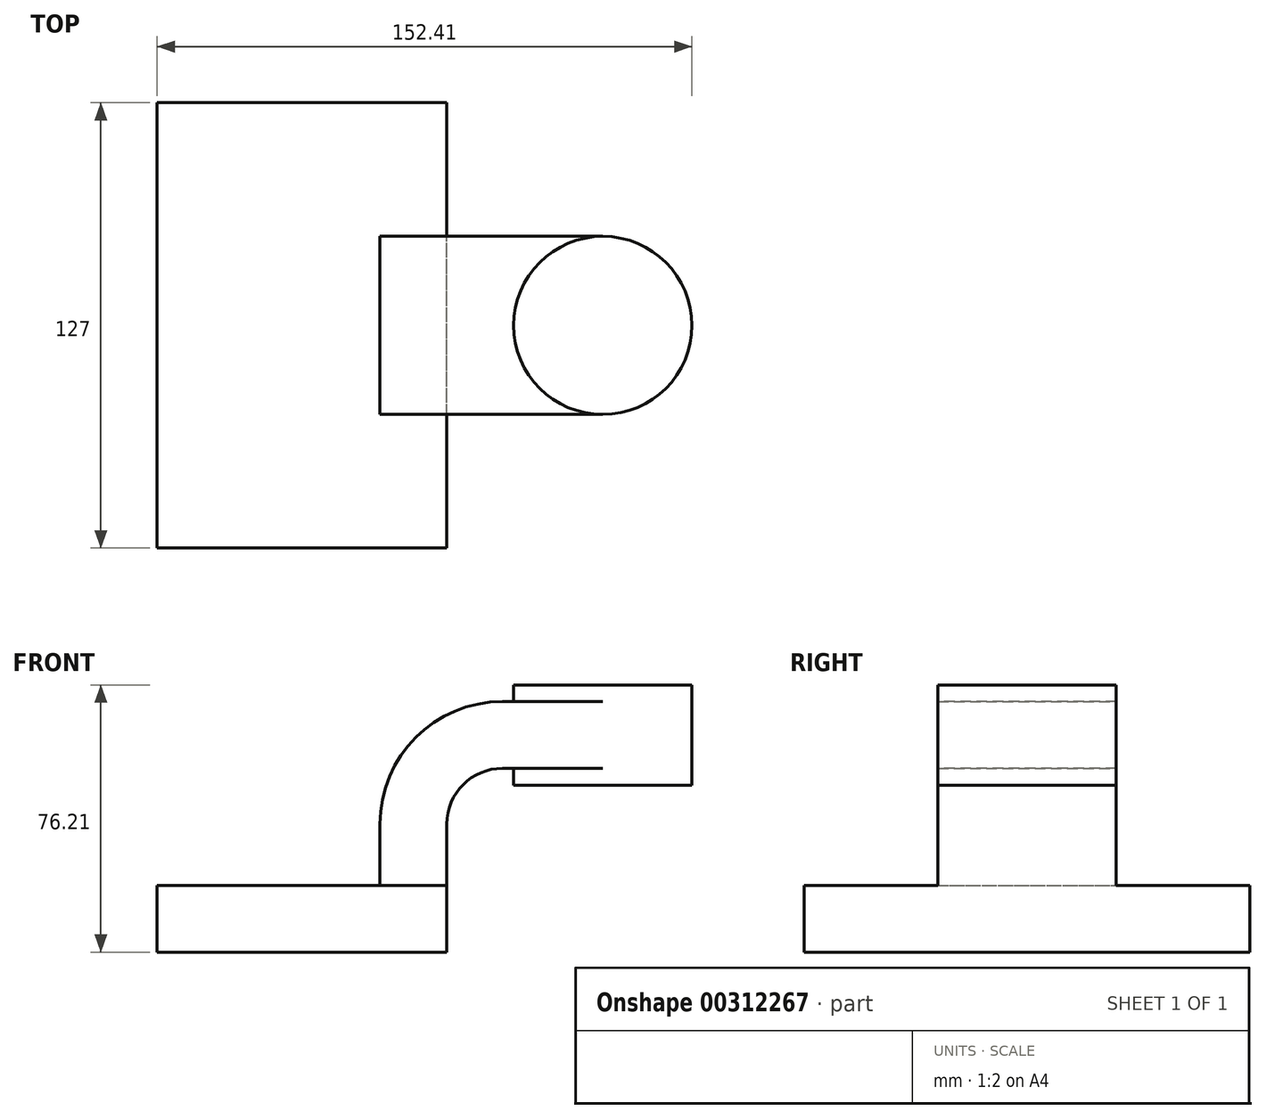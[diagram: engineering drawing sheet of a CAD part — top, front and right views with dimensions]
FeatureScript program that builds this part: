
annotation { "Feature Type Name" : "Feature", "Feature Type Description" : "" }
export const myFeature = defineFeature(function(context is Context, id is Id, definition is map)
    precondition{}
    {
        {
            var Q0;
            Q0=qCreatedBy(makeId("Front.planeOp"),FACE);
            var sketch = newSketch(context, id + "F0", { "sketchPlane" : qUnion([Q0])});
            skLineSegment(sketch, "E0.bottom", {"start": v(41.28, 9.53) * mm, "end": v(-41.28, 9.52) * mm});
            skLineSegment(sketch, "E0.top", {"start": v(41.28, -9.53) * mm, "end": v(-41.28, -9.53) * mm});
            skLineSegment(sketch, "E0.left", {"start": v(41.28, 9.53) * mm, "end": v(41.28, -9.53) * mm});
            skLineSegment(sketch, "E0.right", {"start": v(-41.28, 9.52) * mm, "end": v(-41.28, -9.53) * mm});
            skPoint(sketch, "E0.middle", {"position": v(0, 0) * mm});
            skLineSegment(sketch, "E1.bottom", {"start": v(111.12, 66.68) * mm, "end": v(60.32, 66.68) * mm});
            skLineSegment(sketch, "E1.top", {"start": v(111.12, 38.1) * mm, "end": v(60.32, 38.1) * mm});
            skLineSegment(sketch, "E1.left", {"start": v(111.12, 66.67) * mm, "end": v(111.12, 38.1) * mm});
            skLineSegment(sketch, "E1.right", {"start": v(60.32, 66.67) * mm, "end": v(60.32, 38.1) * mm});
            skPoint(sketch, "E1.middle", {"position": v(85.72, 52.39) * mm});
            skLineSegment(sketch, "E2", {"start": v(41.28, 9.53) * mm, "end": v(41.27, 27) * mm});
            skArc(sketch, "E3", {"start": v(41.27, 27) * mm, "mid": v(45.92, 38.23) * mm, "end": v(57.15, 42.88) * mm});
            skLineSegment(sketch, "E4", {"start": v(57.15, 42.88) * mm, "end": v(85.72, 42.88) * mm});
            skLineSegment(sketch, "E5.0", {"start": v(57.15, 61.93) * mm, "end": v(85.72, 61.93) * mm});
            skArc(sketch, "E5.1", {"start": v(22.22, 27) * mm, "mid": v(32.45, 51.7) * mm, "end": v(57.15, 61.93) * mm});
            skLineSegment(sketch, "E5.2", {"start": v(22.22, 9.52) * mm, "end": v(22.22, 27) * mm});
            skLineSegment(sketch, "E6", {"start": v(85.72, 66.68) * mm, "end": v(85.72, 38.1) * mm});
            skFitSpline(sketch, "E7", {"points": [v(-41.28, 9.52) * mm, v(57.15, 61.93) * mm], "startDerivative": vector(0.43, 51.22) * mm, "endDerivative": vector(140.28, -1.13) * mm});
            skSolve(sketch);
        }
        {
            var Q0;
            Q0=makeQuery(id+"F0.imprint","IMPRINT",FACE,{"disambiguationData":[TD([[makeQuery(id+"F0.imprint","IMPRINT",EDGE,{"derivedFrom":sQuery(id+"F0.wireOp",EDGE,"E0.top")}),-1.0]])]});
            extrude(context, id + "F1", {"entities" : qUnion([Q0]), "endBound" : BoundingType.SYMMETRIC, "depth" : 127 * mm});
        }
        {
            var Q0;
            {var subQ1=sQuery(id+"F0.wireOp",EDGE,"E2");Q0=makeQuery(id+"F0.imprint","IMPRINT",FACE,{"disambiguationData":[TD([[makeQuery(id+"F0.imprint","IMPRINT",EDGE,{"derivedFrom":subQ1}),1.0]])]});}
            var Q1;
            {var subQ0=sQuery(id+"F0.wireOp",EDGE,"E5.0");var subQ1=sQuery(id+"F0.wireOp",EDGE,"E1.right");var subQ2=makeQuery(id+"F0.imprint","INTERSECT",VERTEX,{"derivedFrom":[subQ1,subQ0]});Q1=makeQuery(id+"F0.imprint","IMPRINT",FACE,{"disambiguationData":[TD([[makeQuery(id+"F0.imprint","IMPRINT",EDGE,{"disambiguationData":[TD([[subQ2,-1.0]])],"derivedFrom":subQ1}),1.0]])]});}
            extrude(context, id + "F2", {"entities" : qUnion([Q0, Q1]), "operationType" : NewBodyOperationType.ADD, "endBound" : BoundingType.SYMMETRIC, "depth" : 50.8 * mm});
        }
        {
            var Q0;
            Q0=makeQuery(id+"F0.imprint","IMPRINT",FACE,{"disambiguationData":[TD([[makeQuery(id+"F0.imprint","IMPRINT",EDGE,{"derivedFrom":sQuery(id+"F0.wireOp",EDGE,"E5.1")}),1.0]])]});
            extrude(context, id + "F3", {"entities" : qUnion([Q0]), "operationType" : NewBodyOperationType.ADD, "endBound" : BoundingType.SYMMETRIC, "depth" : 15.88 * mm});
        }
        {
            var Q0;
            {var subQ4=sQuery(id+"F0.wireOp",EDGE,"E1.left");Q0=makeQuery(id+"F0.imprint","IMPRINT",FACE,{"disambiguationData":[TD([[makeQuery(id+"F0.imprint","IMPRINT",EDGE,{"derivedFrom":subQ4}),-1.0]])]});}
            var Q1;
            Q1=sQuery(id+"F0.wireOp",EDGE,"E6");
            revolve(context, id + "F4", {"operationType" : NewBodyOperationType.ADD, "entities" : qUnion([Q0]), "axis" : qUnion([Q1]), "revolveType" : RevolveType.FULL});
        }
    });
